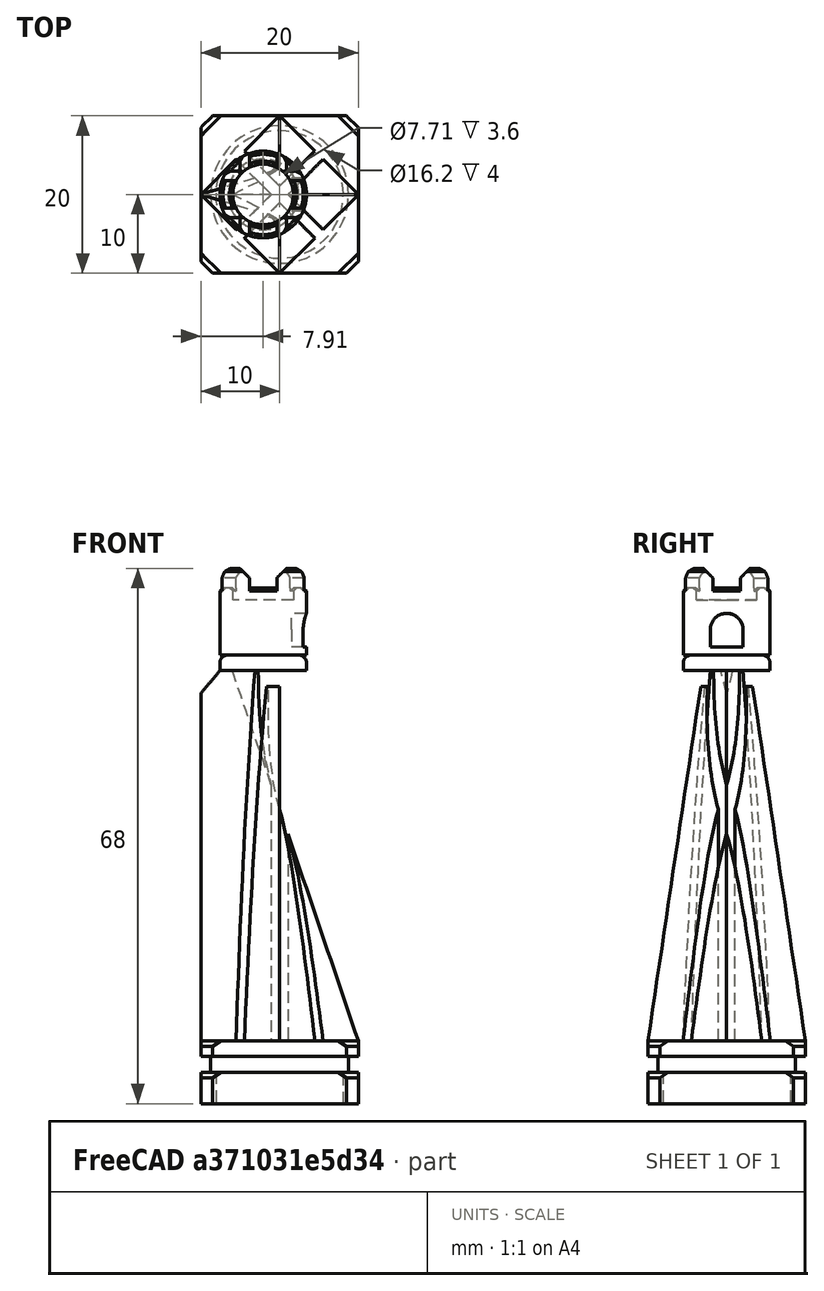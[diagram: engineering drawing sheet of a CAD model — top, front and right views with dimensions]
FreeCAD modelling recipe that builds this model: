
FCSTD DOCUMENT  (FreeCAD 0.21R33771 (Git))
Label: Queen
License: All rights reserved
LicenseURL: http://en.wikipedia.org/wiki/All_rights_reserved
objects: Sketcher::SketchObject×14, PartDesign::Pocket×7, PartDesign::Chamfer×6, PartDesign::Pad×5, Spreadsheet::Sheet×1, PartDesign::AdditiveLoft×1, PartDesign::Draft×1, PartDesign::Fillet×1, PartDesign::Body×1, App::Part×1
note: 57 computed .brp shape members not serialized (recipe doc carries the construction recipe); baked Part::Feature solids carry a one-line shape summary decoded from their .brp

FEATURE [Spreadsheet::Sheet] Spreadsheet  label="p"
  cells = A1='base_hole; B1(base_hole)=16; A2='base_clearance; B2(base_clearance)=0.2; A3='base_depth; B3(base_depth)=4; A4='base_spacer_depth; B4(base_spacer_depth)=2; A5='base_chamfer; B5(base_chamfer)=1.5; A6='base_total_depth; B6(base_total_depth)==B3 + base_spacer_depth * 2; A8='body_height; B8(pawn_body_height)=55; A10='base_wall; B10(base_wall)=4; A12='loft_top; B12(loft_top)=2; A14='platform_diameter; B14(platform_diameter)=11; A15='platform_offset; B15(platform_offset)=2.09
FEATURE [Sketcher::SketchObject] Sketch
  FullyConstrained = true
  MapMode = 5
  Support = -> [XY_Plane001]
  expr: Constraints[10] = <<p>>.base_hole + Spreadsheet.base_wall
  expr: Constraints[11] = <<p>>.base_hole + Spreadsheet.base_wall
  expr: Constraints[1] = <<p>>.base_hole + <<p>>.base_clearance
  sketch-geometry (5):
    g0: Circle CenterX=0 CenterY=0 CenterZ=0 NormalX=0 NormalY=0 NormalZ=1 AngleXU=0 Radius=8.1
    g1: LineSegment StartX=-10 StartY=10 StartZ=0 EndX=10 EndY=10 EndZ=0
    g2: LineSegment StartX=10 StartY=10 StartZ=0 EndX=10 EndY=-10 EndZ=0
    g3: LineSegment StartX=10 StartY=-10 StartZ=0 EndX=-10 EndY=-10 EndZ=0
    g4: LineSegment StartX=-10 StartY=-10 StartZ=0 EndX=-10 EndY=10 EndZ=0
  constraints (13):
    c: Coincident(g0,g-1)
    c: Diameter(g0) = 16.2
    c: Coincident(g1,g2)
    c: Coincident(g2,g3)
    c: Coincident(g3,g4)
    c: Coincident(g4,g1)
    c: Horizontal(g1)
    c: Horizontal(g3)
    c: Vertical(g2)
    c: Vertical(g4)
    c: DistanceY(g4,g4) = 20
    c: DistanceX(g1,g1) = 20
    c: Symmetric(g1,g3,g0)
FEATURE [PartDesign::Pad] Pad  label="BasePad"
  Direction = (0,0,1)
  Length = 4
  Length2 = 10
  Profile = -> Sketch
  ReferenceAxis = -> Sketch [N_Axis]
  Type = 0
  expr: Length = <<p>>.base_depth
FEATURE [PartDesign::Chamfer] Chamfer  label="BasePadChamfer"
  Angle = 45
  Base = -> Pad [Edge8,Edge5,Edge2,Edge1]
  BaseFeature = -> Pad
  ChamferType = 0
  FlipDirection = false
  Size = 1.5
  Size2 = 1
  SupportTransform = false
  UseAllEdges = false
  expr: Size = <<p>>.base_chamfer
FEATURE [Sketcher::SketchObject] Sketch001
  FullyConstrained = true
  MapMode = 5
  Placement = pos=(0,0,4) rot=(0,0,1;0rad)
  Support = -> [Chamfer]
  expr: Constraints[1] = <<p>>.base_hole + 1.5
  sketch-geometry (1):
    g0: Circle CenterX=0 CenterY=0 CenterZ=0 NormalX=0 NormalY=0 NormalZ=1 AngleXU=0 Radius=8.75
  constraints (2):
    c: Coincident(g0,g-1)
    c: Diameter(g0) = 17.5
FEATURE [PartDesign::Pad] Pad001  label="BasePadTopper"
  BaseFeature = -> Chamfer
  Direction = (0,0,1)
  Length = 2
  Length2 = 10
  Profile = -> Sketch001
  ReferenceAxis = -> Sketch001 [N_Axis]
  Type = 0
  expr: Length = <<p>>.base_spacer_depth
FEATURE [Sketcher::SketchObject] Sketch002
  FullyConstrained = true
  MapMode = 5
  Placement = pos=(0,0,6) rot=(0,0,1;0rad)
  Support = -> [Pad001]
  expr: Constraints[8] = <<p>>.base_hole + Spreadsheet.base_wall
  expr: Constraints[9] = <<p>>.base_hole + Spreadsheet.base_wall
  sketch-geometry (4):
    g0: LineSegment StartX=-10 StartY=10 StartZ=0 EndX=10 EndY=10 EndZ=0
    g1: LineSegment StartX=10 StartY=10 StartZ=0 EndX=10 EndY=-10 EndZ=0
    g2: LineSegment StartX=10 StartY=-10 StartZ=0 EndX=-10 EndY=-10 EndZ=0
    g3: LineSegment StartX=-10 StartY=-10 StartZ=0 EndX=-10 EndY=10 EndZ=0
  constraints (11):
    c: Coincident(g0,g1)
    c: Coincident(g1,g2)
    c: Coincident(g2,g3)
    c: Coincident(g3,g0)
    c: Horizontal(g0)
    c: Horizontal(g2)
    c: Vertical(g1)
    c: Vertical(g3)
    c: DistanceY(g3,g3) = 20
    c: DistanceX(g0,g0) = 20
    c: Symmetric(g0,g2,g-1)
FEATURE [PartDesign::Pad] Pad002  label="BaseBodyBase"
  BaseFeature = -> Pad001
  Direction = (0,0,1)
  Length = 2
  Length2 = 10
  Profile = -> Sketch002
  ReferenceAxis = -> Sketch002 [N_Axis]
  Type = 0
  expr: Length = <<p>>.base_spacer_depth
FEATURE [PartDesign::Chamfer] Chamfer001  label="BaseBodyBaseChamfer"
  Angle = 45
  Base = -> Pad002 [Edge8,Edge2,Edge1,Edge5]
  BaseFeature = -> Pad002
  ChamferType = 0
  FlipDirection = false
  Size = 1.5
  Size2 = 1
  SupportTransform = false
  UseAllEdges = false
  expr: Size = <<p>>.base_chamfer
FEATURE [Sketcher::SketchObject] Sketch003
  FullyConstrained = true
  MapMode = 5
  Placement = pos=(0,0,8) rot=(0,0,1;0rad)
  Support = -> [Chamfer001]
  expr: Constraints[10] = (<<p>>.base_hole + Spreadsheet.base_wall) / 2
  expr: Constraints[11] = <<p>>.base_hole + Spreadsheet.base_wall
  expr: Constraints[8] = (<<p>>.base_hole + Spreadsheet.base_wall) / 2
  expr: Constraints[9] = <<p>>.base_hole + Spreadsheet.base_wall
  sketch-geometry (4):
    g0: LineSegment StartX=0 StartY=10 StartZ=0 EndX=-10 EndY=0 EndZ=0
    g1: LineSegment StartX=-10 StartY=0 StartZ=0 EndX=0 EndY=-10 EndZ=0
    g2: LineSegment StartX=0 StartY=-10 StartZ=0 EndX=10 EndY=0 EndZ=0
    g3: LineSegment StartX=10 StartY=0 StartZ=0 EndX=0 EndY=10 EndZ=0
  constraints (12):
    c: PointOnObject(g0,g-2)
    c: PointOnObject(g0,g-1)
    c: Coincident(g0,g1)
    c: PointOnObject(g1,g-2)
    c: Coincident(g1,g2)
    c: PointOnObject(g2,g-1)
    c: Coincident(g2,g3)
    c: Coincident(g3,g0)
    c: DistanceX(g0,g-1) = 10
    c: DistanceX(g0,g2) = 20
    c: DistanceY(g-1,g0) = 10
    c: DistanceY(g1,g0) = 20
FEATURE [Sketcher::SketchObject] Sketch004
  FullyConstrained = true
  MapMode = 5
  Placement = pos=(0,0,55) rot=(0,0,1;0rad)
  expr: .Placement.Base.z = <<p>>.pawn_body_height
  expr: Constraints[10] = <<p>>.loft_top * 3
  expr: Constraints[11] = <<p>>.loft_top * 3 / 2
  expr: Constraints[8] = <<p>>.loft_top * 2
  expr: Constraints[9] = <<p>>.loft_top * 3
  sketch-geometry (4):
    g0: LineSegment StartX=0 StartY=3 StartZ=0 EndX=-10 EndY=0 EndZ=0
    g1: LineSegment StartX=-10 StartY=0 StartZ=0 EndX=0 EndY=-3 EndZ=0
    g2: LineSegment StartX=0 StartY=-3 StartZ=0 EndX=-6 EndY=0 EndZ=0
    g3: LineSegment StartX=-6 StartY=0 StartZ=0 EndX=0 EndY=3 EndZ=0
  constraints (12):
    c: PointOnObject(g0,g-2)
    c: PointOnObject(g0,g-1)
    c: Coincident(g0,g1)
    c: PointOnObject(g1,g-2)
    c: Coincident(g1,g2)
    c: PointOnObject(g2,g-1)
    c: Coincident(g2,g3)
    c: Coincident(g3,g0)
    c: DistanceX(g0,g2) = 4
    c: DistanceY(g1,g0) = 6
    c: DistanceX(g2,g-1) = 6
    c: DistanceY(g-1,g0) = 3
FEATURE [PartDesign::AdditiveLoft] AdditiveLoft
  BaseFeature = -> Chamfer001
  Closed = false
  Profile = -> Sketch003
  Ruled = false
  Sections = -> [Sketch004]
FEATURE [Sketcher::SketchObject] Sketch005
  FullyConstrained = true
  MapMode = 5
  Placement = pos=(-9.25,9.25,0) rot=(-0.281085,0.678598,0.678598;3.68962rad)
  Support = -> [AdditiveLoft]
  expr: Constraints[10] = <<p>>.base_total_depth
  expr: Constraints[11] = <<p>>.pawn_body_height - <<p>>.base_total_depth
  expr: Constraints[8] = <<p>>.base_chamfer
  expr: Constraints[9] = <<p>>.base_chamfer / 2
  sketch-geometry (4):
    g0: LineSegment StartX=-0.75 StartY=55 StartZ=0 EndX=0.75 EndY=55 EndZ=0
    g1: LineSegment StartX=0.75 StartY=55 StartZ=0 EndX=0.75 EndY=8 EndZ=0
    g2: LineSegment StartX=0.75 StartY=8 StartZ=0 EndX=-0.75 EndY=8 EndZ=0
    g3: LineSegment StartX=-0.75 StartY=8 StartZ=0 EndX=-0.75 EndY=55 EndZ=0
  constraints (12):
    c: Coincident(g0,g1)
    c: Coincident(g1,g2)
    c: Coincident(g2,g3)
    c: Coincident(g3,g0)
    c: Horizontal(g0)
    c: Horizontal(g2)
    c: Vertical(g1)
    c: Vertical(g3)
    c: DistanceX(g2,g2) = 1.5
    c: DistanceX(g2,g-1) = 0.75
    c: DistanceY(g-1,g2) = 8
    c: DistanceY(g1,g1) = 47
FEATURE [PartDesign::Pocket] Pocket  label="SidePocket1"
  BaseFeature = -> AdditiveLoft
  Direction = (0.707107,-0.707107,0)
  Length = 5
  Length2 = 5
  Profile = -> Sketch005
  ReferenceAxis = -> Sketch005 [N_Axis]
  Type = 1
FEATURE [Sketcher::SketchObject] Sketch006
  FullyConstrained = true
  MapMode = 5
  Placement = pos=(-9.25,-9.25,0) rot=(0.862856,-0.357407,-0.357407;1.71777rad)
  Support = -> [AdditiveLoft]
  expr: Constraints[10] = <<p>>.base_total_depth
  expr: Constraints[11] = <<p>>.pawn_body_height - <<p>>.base_total_depth
  expr: Constraints[8] = <<p>>.base_chamfer
  expr: Constraints[9] = <<p>>.base_chamfer / 2
  sketch-geometry (4):
    g0: LineSegment StartX=-0.75 StartY=55 StartZ=0 EndX=0.75 EndY=55 EndZ=0
    g1: LineSegment StartX=0.75 StartY=55 StartZ=0 EndX=0.75 EndY=8 EndZ=0
    g2: LineSegment StartX=0.75 StartY=8 StartZ=0 EndX=-0.75 EndY=8 EndZ=0
    g3: LineSegment StartX=-0.75 StartY=8 StartZ=0 EndX=-0.75 EndY=55 EndZ=0
  constraints (12):
    c: Coincident(g0,g1)
    c: Coincident(g1,g2)
    c: Coincident(g2,g3)
    c: Coincident(g3,g0)
    c: Horizontal(g0)
    c: Horizontal(g2)
    c: Vertical(g1)
    c: Vertical(g3)
    c: DistanceX(g2,g2) = 1.5
    c: DistanceX(g2,g-1) = 0.75
    c: DistanceY(g-1,g2) = 8
    c: DistanceY(g1,g1) = 47
FEATURE [PartDesign::Pocket] Pocket001  label="SidePocket2"
  BaseFeature = -> Pocket
  Direction = (0.707107,0.707107,0)
  Length = 5
  Length2 = 5
  Profile = -> Sketch006
  ReferenceAxis = -> Sketch006 [N_Axis]
  Type = 1
FEATURE [Sketcher::SketchObject] Sketch007
  FullyConstrained = true
  MapMode = 5
  Placement = pos=(0,0,55) rot=(0,0,1;0rad)
  Support = -> [Pocket001]
  expr: Constraints[1] = <<p>>.platform_diameter
  expr: Constraints[2] = <<p>>.platform_offset
  sketch-geometry (1):
    g0: Circle CenterX=-2.09 CenterY=0 CenterZ=0 NormalX=0 NormalY=0 NormalZ=1 AngleXU=0 Radius=5.5
  constraints (3):
    c: PointOnObject(g0,g-1)
    c: Diameter(g0) = 11
    c: DistanceX(g0,g-1) = 2.09
FEATURE [PartDesign::Pad] Pad003  label="PlatformPad"
  BaseFeature = -> Pocket001
  Direction = (0,0,1)
  Length = 2
  Length2 = 10
  Profile = -> Sketch007
  ReferenceAxis = -> Sketch007 [N_Axis]
  Type = 0
FEATURE [PartDesign::Draft] Draft  label="RearDraft"
  Angle = 50
  Base = -> Pad003 [Face49]
  BaseFeature = -> Pad003
  SupportTransform = false
FEATURE [PartDesign::Chamfer] Chamfer002  label="BaseChamfers"
  Angle = 45
  Base = -> Draft [Edge34,Edge38,Edge20,Edge16,Edge67,Edge71,Edge72,Edge68]
  BaseFeature = -> Draft
  ChamferType = 0
  FlipDirection = false
  Size = 0.75
  Size2 = 1
  SupportTransform = false
  UseAllEdges = false
FEATURE [PartDesign::Fillet] Fillet  label="PlatformChamfer"
  Base = -> Chamfer002 [Edge159]
  BaseFeature = -> Chamfer002
  Radius = 1
  SupportTransform = false
  UseAllEdges = false
FEATURE [Sketcher::SketchObject] Sketch008
  FullyConstrained = true
  MapMode = 5
  Placement = pos=(0,0,57) rot=(0,0,1;0rad)
  Support = -> [Fillet]
  expr: Constraints[1] = <<p>>.platform_diameter
  expr: Constraints[2] = <<p>>.platform_offset
  sketch-geometry (1):
    g0: Circle CenterX=-2.09 CenterY=0 CenterZ=0 NormalX=0 NormalY=0 NormalZ=1 AngleXU=0 Radius=5.5
  constraints (3):
    c: PointOnObject(g0,g-1)
    c: Diameter(g0) = 11
    c: DistanceX(g0,g-1) = 2.09
FEATURE [PartDesign::Pad] Pad004  label="CrownPad"
  BaseFeature = -> Fillet
  Direction = (0,0,1)
  Length = 11
  Length2 = 10
  Profile = -> Sketch008
  ReferenceAxis = -> Sketch008 [N_Axis]
  Type = 0
  expr: Length = <<p>>.platform_diameter
FEATURE [Sketcher::SketchObject] Sketch009
  FullyConstrained = true
  MapMode = 5
  Placement = pos=(0,0,68) rot=(0,0,1;0rad)
  Support = -> [Pad004]
  expr: Constraints[1] = <<p>>.platform_offset
  sketch-geometry (1):
    g0: Circle CenterX=-2.09 CenterY=0 CenterZ=0 NormalX=0 NormalY=0 NormalZ=1 AngleXU=0 Radius=3.855
  constraints (3):
    c: PointOnObject(g0,g-1)
    c: DistanceX(g0,g-1) = 2.09
    c: Diameter(g0) = 7.71
FEATURE [PartDesign::Pocket] Pocket002  label="CrownPocket"
  BaseFeature = -> Pad004
  Direction = (0,0,-1)
  Length = 4
  Length2 = 5
  Profile = -> Sketch009
  ReferenceAxis = -> Sketch009 [N_Axis]
  Type = 0
FEATURE [Sketcher::SketchObject] Sketch010
  FullyConstrained = true
  MapMode = 5
  Placement = pos=(10,0,0) rot=(0.57735,0.57735,0.57735;2.0944rad)
  Support = -> [Pocket002]
  sketch-geometry (4):
    g0: LineSegment StartX=-1.75 StartY=70 StartZ=0 EndX=1.75 EndY=70 EndZ=0
    g1: LineSegment StartX=1.75 StartY=70 StartZ=0 EndX=1.75 EndY=65.5 EndZ=0
    g2: LineSegment StartX=1.75 StartY=65.5 StartZ=0 EndX=-1.75 EndY=65.5 EndZ=0
    g3: LineSegment StartX=-1.75 StartY=65.5 StartZ=0 EndX=-1.75 EndY=70 EndZ=0
  constraints (12):
    c: Coincident(g0,g1)
    c: Coincident(g1,g2)
    c: Coincident(g2,g3)
    c: Coincident(g3,g0)
    c: Horizontal(g0)
    c: Horizontal(g2)
    c: Vertical(g1)
    c: Vertical(g3)
    c: DistanceY(g1,g1) = 4.5
    c: DistanceX(g0,g0) = 3.5
    c: DistanceX(g2,g-1) = 1.75
    c: DistanceY(g-1,g0) = 70
FEATURE [Sketcher::SketchObject] Sketch011
  FullyConstrained = true
  MapMode = 5
  Placement = pos=(0,10,0) rot=(0,0.707107,0.707107;3.14159rad)
  Support = -> [Pocket002]
  sketch-geometry (4):
    g0: LineSegment StartX=0.34 StartY=70 StartZ=0 EndX=3.84 EndY=70 EndZ=0
    g1: LineSegment StartX=3.84 StartY=70 StartZ=0 EndX=3.84 EndY=65.5 EndZ=0
    g2: LineSegment StartX=3.84 StartY=65.5 StartZ=0 EndX=0.34 EndY=65.5 EndZ=0
    g3: LineSegment StartX=0.34 StartY=65.5 StartZ=0 EndX=0.34 EndY=70 EndZ=0
  constraints (12):
    c: Coincident(g0,g1)
    c: Coincident(g1,g2)
    c: Coincident(g2,g3)
    c: Coincident(g3,g0)
    c: Horizontal(g0)
    c: Horizontal(g2)
    c: Vertical(g1)
    c: Vertical(g3)
    c: DistanceY(g3,g3) = 4.5
    c: DistanceX(g0,g0) = 3.5
    c: DistanceX(g-1,g2) = 0.34
    c: DistanceY(g-1,g2) = 65.5
FEATURE [PartDesign::Pocket] Pocket003  label="FacePocket"
  BaseFeature = -> Pocket002
  Direction = (-1,0,0)
  Length = 5
  Length2 = 5
  Profile = -> Sketch010
  ReferenceAxis = -> Sketch010 [N_Axis]
  Type = 1
FEATURE [PartDesign::Pocket] Pocket004  label="SidePocket"
  BaseFeature = -> Pocket003
  Direction = (0,-1,2e-16)
  Length = 5
  Length2 = 5
  Profile = -> Sketch011
  ReferenceAxis = -> Sketch011 [N_Axis]
  Type = 1
FEATURE [PartDesign::Chamfer] Chamfer003  label="LowerChamfer"
  Angle = 45
  Base = -> Pocket004 [Edge14,Edge47,Edge2,Edge21,Edge22,Edge18,Edge30,Edge6,Edge38,Edge10]
  BaseFeature = -> Pocket004
  ChamferType = 0
  FlipDirection = false
  Size = 0.4
  Size2 = 1
  SupportTransform = false
  UseAllEdges = false
FEATURE [PartDesign::Chamfer] Chamfer004
  Angle = 45
  Base = -> Chamfer003 [Edge19,Edge68,Edge79,Edge24,Edge51,Edge12,Edge7,Edge40]
  BaseFeature = -> Chamfer003
  ChamferType = 0
  FlipDirection = false
  Size = 0.4
  Size2 = 1
  SupportTransform = false
  UseAllEdges = false
FEATURE [PartDesign::Chamfer] Chamfer005
  Angle = 45
  Base = -> Chamfer004 [Edge53,Edge71,Edge89,Edge97,Edge79,Edge62,Edge29,Edge41]
  BaseFeature = -> Chamfer004
  ChamferType = 0
  FlipDirection = false
  Size = 1.2
  Size2 = 1
  SupportTransform = false
  UseAllEdges = false
FEATURE [Sketcher::SketchObject] Sketch012
  FullyConstrained = true
  MapMode = 5
  Placement = pos=(10,0,0) rot=(0.57735,0.57735,0.57735;2.0944rad)
  Support = -> [Chamfer005]
  sketch-geometry (5):
    g0: LineSegment StartX=2.0855 StartY=60.211 StartZ=0 EndX=2.0855 EndY=58 EndZ=0
    g1: LineSegment StartX=2.0855 StartY=58 StartZ=0 EndX=-2.0855 EndY=58 EndZ=0
    g2: LineSegment StartX=-2.0855 StartY=58 StartZ=0 EndX=-2.0855 EndY=60.211 EndZ=0
    g3: ArcOfCircle CenterX=0 CenterY=60.211 CenterZ=0 NormalX=0 NormalY=0 NormalZ=1 AngleXU=0 Radius=2.0855 StartAngle=1.5708 EndAngle=3.14159
    g4: ArcOfCircle CenterX=0 CenterY=60.211 CenterZ=0 NormalX=0 NormalY=0 NormalZ=1 AngleXU=0 Radius=2.0855 StartAngle=2e-16 EndAngle=1.5708
  constraints (14):
    c: Coincident(g0,g1)
    c: Coincident(g1,g2)
    c: Horizontal(g1)
    c: Vertical(g0)
    c: Vertical(g2)
    c: Tangent(g2,g3) = 1.5708
    c: Tangent(g0,g4) = 1.5708
    c: Coincident(g3,g4)
    c: DistanceX(g3,g3) = 0
    c: DistanceX(g3,g-1) = 0
    c: Coincident(g4,g3)
    c: DistanceX(g2,g0) = 4.171
    c: DistanceY(g0,g0) = 2.211
    c: DistanceY(g-1,g1) = 58
FEATURE [PartDesign::Pocket] Pocket005
  BaseFeature = -> Chamfer005
  Direction = (-1,0,0)
  Length = 8.5
  Length2 = 5
  Profile = -> Sketch012
  ReferenceAxis = -> Sketch012 [N_Axis]
  Type = 0
FEATURE [Sketcher::SketchObject] Sketch013
  FullyConstrained = false
  MapMode = 5
  Placement = pos=(0,-10,0) rot=(1,0,0;1.5708rad)
  Support = -> [Pocket005]
  expr: Constraints[8] = <<p>>.pawn_body_height
  sketch-geometry (4):
    g0: LineSegment StartX=0.546696 StartY=53 StartZ=0 EndX=-1.9533 EndY=53 EndZ=0
    g1: LineSegment StartX=-1.9533 StartY=53 StartZ=0 EndX=-1.9533 EndY=55 EndZ=0
    g2: LineSegment StartX=-1.9533 StartY=55 StartZ=0 EndX=0.546696 EndY=55 EndZ=0
    g3: LineSegment StartX=0.546696 StartY=55 StartZ=0 EndX=0.546696 EndY=53 EndZ=0
  constraints (11):
    c: Coincident(g0,g1)
    c: Coincident(g1,g2)
    c: Coincident(g2,g3)
    c: Coincident(g3,g0)
    c: Horizontal(g0)
    c: Horizontal(g2)
    c: Vertical(g1)
    c: Vertical(g3)
    c: DistanceY(g-1,g1) = 55
    c: DistanceX(g2,g2) = 2.5
    c: DistanceY(g3,g3) = 2
FEATURE [PartDesign::Pocket] Pocket006
  BaseFeature = -> Pocket005
  Direction = (0,1,-2e-16)
  Length = 5
  Length2 = 5
  Profile = -> Sketch013
  ReferenceAxis = -> Sketch013 [N_Axis]
  Type = 1
FEATURE [PartDesign::Body] Body  label="QueenBody"
  Group = -> [Sketch,Pad,Chamfer,Sketch001,Pad001,Sketch002,Pad002,Chamfer001,Sketch003,Sketch004,AdditiveLoft,Sketch005,Pocket,Sketch006,Pocket001,Sketch007,Pad003,Draft,Chamfer002,Fillet,Sketch008,Pad004,Sketch009,Pocket002,Sketch010,Sketch011,Pocket003,Pocket004,Chamfer003,Chamfer004,Chamfer005,Sketch012,Pocket005,Sketch013,Pocket006]
  Origin = -> Origin001
  Tip = -> Pocket006
FEATURE [App::Part] Part  label="QueenPart"
  Group = -> [Body]
  Origin = -> Origin
